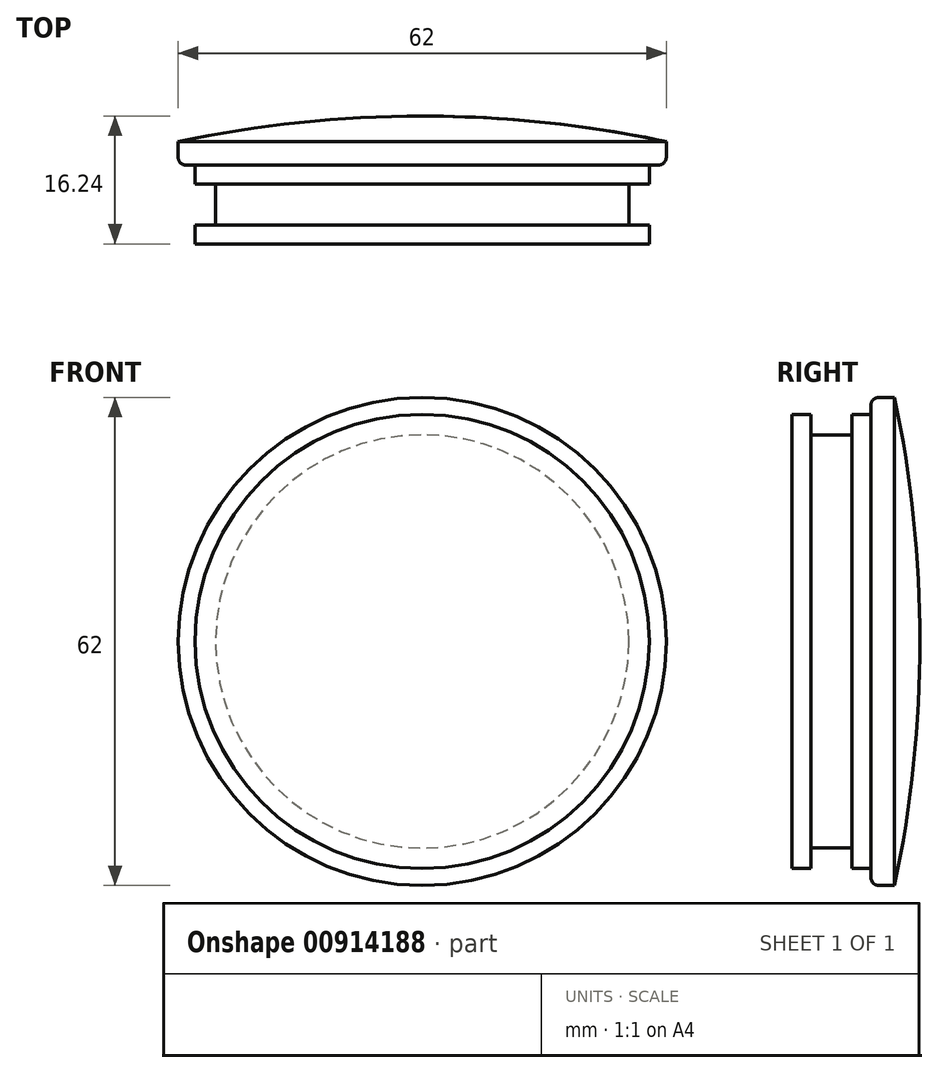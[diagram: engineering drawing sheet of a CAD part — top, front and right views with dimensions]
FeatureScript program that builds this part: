
annotation { "Feature Type Name" : "Feature", "Feature Type Description" : "" }
export const myFeature = defineFeature(function(context is Context, id is Id, definition is map)
    precondition{}
    {
        {
            var Q0;
            Q0=qCreatedBy(makeId("Top.planeOp"),FACE);
            var sketch = newSketch(context, id + "F0", { "sketchPlane" : qUnion([Q0])});
            skLineSegment(sketch, "E0", {"start": v(28.85, 0) * mm, "end": v(28.85, 2.4) * mm});
            skLineSegment(sketch, "E1", {"start": v(28.85, 2.4) * mm, "end": v(26.25, 2.4) * mm});
            skLineSegment(sketch, "E2", {"start": v(26.25, 2.4) * mm, "end": v(26.25, 7.6) * mm});
            skLineSegment(sketch, "E3", {"start": v(26.25, 7.6) * mm, "end": v(28.85, 7.6) * mm});
            skLineSegment(sketch, "E4", {"start": v(0, 0) * mm, "end": v(28.85, 0) * mm});
            skLineSegment(sketch, "E5", {"start": v(28.85, 7.6) * mm, "end": v(28.85, 10) * mm});
            skLineSegment(sketch, "E6", {"start": v(28.85, 10) * mm, "end": v(30, 10) * mm});
            skLineSegment(sketch, "E7", {"start": v(31, 11) * mm, "end": v(31, 13) * mm});
            skPoint(sketch, "E8.visualSharp", {"position": v(31, 10) * mm});
            skArc(sketch, "E8.filletArc", {"start": v(30, 10) * mm, "mid": v(30.7, 10.3) * mm, "end": v(31, 11) * mm});
            skArc(sketch, "E9", {"start": v(31, 13) * mm, "mid": v(15.58, 15.43) * mm, "end": v(0, 16.24) * mm});
            skPoint(sketch, "E9.third.point", {"position": v(0, -283.76) * mm});
            skLineSegment(sketch, "E10", {"start": v(0, 16.24) * mm, "end": v(0, 0) * mm});
            skSolve(sketch);
        }
        {
            var Q0;
            Q0=makeQuery(id+"F0.imprint","IMPRINT",FACE,{"disambiguationData":[TD([[makeQuery(id+"F0.imprint","IMPRINT",EDGE,{"derivedFrom":sQuery(id+"F0.wireOp",EDGE,"E0")}),1.0]])]});
            var Q1;
            Q1=sQuery(id+"F0.wireOp",EDGE,"E9");
            var Q2;
            Q2=sQuery(id+"F0.wireOp",EDGE,"E7");
            var Q3;
            Q3=sQuery(id+"F0.wireOp",EDGE,"E8.filletArc");
            var Q4;
            Q4=sQuery(id+"F0.wireOp",EDGE,"E6");
            var Q5;
            Q5=sQuery(id+"F0.wireOp",EDGE,"E5");
            var Q6;
            Q6=sQuery(id+"F0.wireOp",EDGE,"E3");
            var Q7;
            Q7=sQuery(id+"F0.wireOp",EDGE,"E2");
            var Q8;
            Q8=sQuery(id+"F0.wireOp",EDGE,"E1");
            var Q9;
            Q9=sQuery(id+"F0.wireOp",EDGE,"E0");
            var Q10;
            Q10=sQuery(id+"F0.wireOp",EDGE,"E4");
            var Q11;
            Q11=sQuery(id+"F0.wireOp",EDGE,"E10");
            revolve(context, id + "F1", {"surfaceOperationType" : NewSurfaceOperationType.NEW, "entities" : qUnion([Q0]), "surfaceEntities" : qUnion([Q1, Q2, Q3, Q4, Q5, Q6, Q7, Q8, Q9, Q10]), "axis" : qUnion([Q11]), "revolveType" : RevolveType.FULL});
        }
    });
